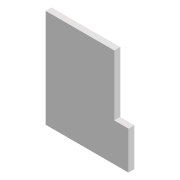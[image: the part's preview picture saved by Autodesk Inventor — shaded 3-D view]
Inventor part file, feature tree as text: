
AUTODESK INVENTOR PART (.ipt)
format: ipt  version: 2022 (Build 260153000, 153)  size: 93,184 bytes
history: native  units: mm
features: reference x3, other x3, extrude x2, sketch x2, projected_geometry x1
ambient origin geometry x8: Origin, YZ Plane, XZ Plane, XY Plane, X Axis, Y Axis, Z Axis, Center Point
bodies: Volumenkörper1 (feature_tree)
feature tree (11):
  extrude  "Extrusion1"  Depth=25.0mm
  extrude  "Extrusion2"  Depth=1.5mm TaperAngle=0.0deg
  sketch  "Skizze1"  dims[d0=21.0mm d1=25.0mm]
  reference  "Referenz1"
  sketch  "Skizze2"  dims[d2=3.6mm d4=1.5mm d5=0.0mm d6=1.75mm d7=10.0mm d8=0.0mm]
  reference  "Referenz2"
  projected_geometry  "Projizierte Kontur1"
  reference  "Referenz3"
  other  "Baugruppe1"
  other  "00_huawei_p30_Objectivelensassembly:1"
  other  "Assembly_Huawei_P30_Scanninglens.iam"
